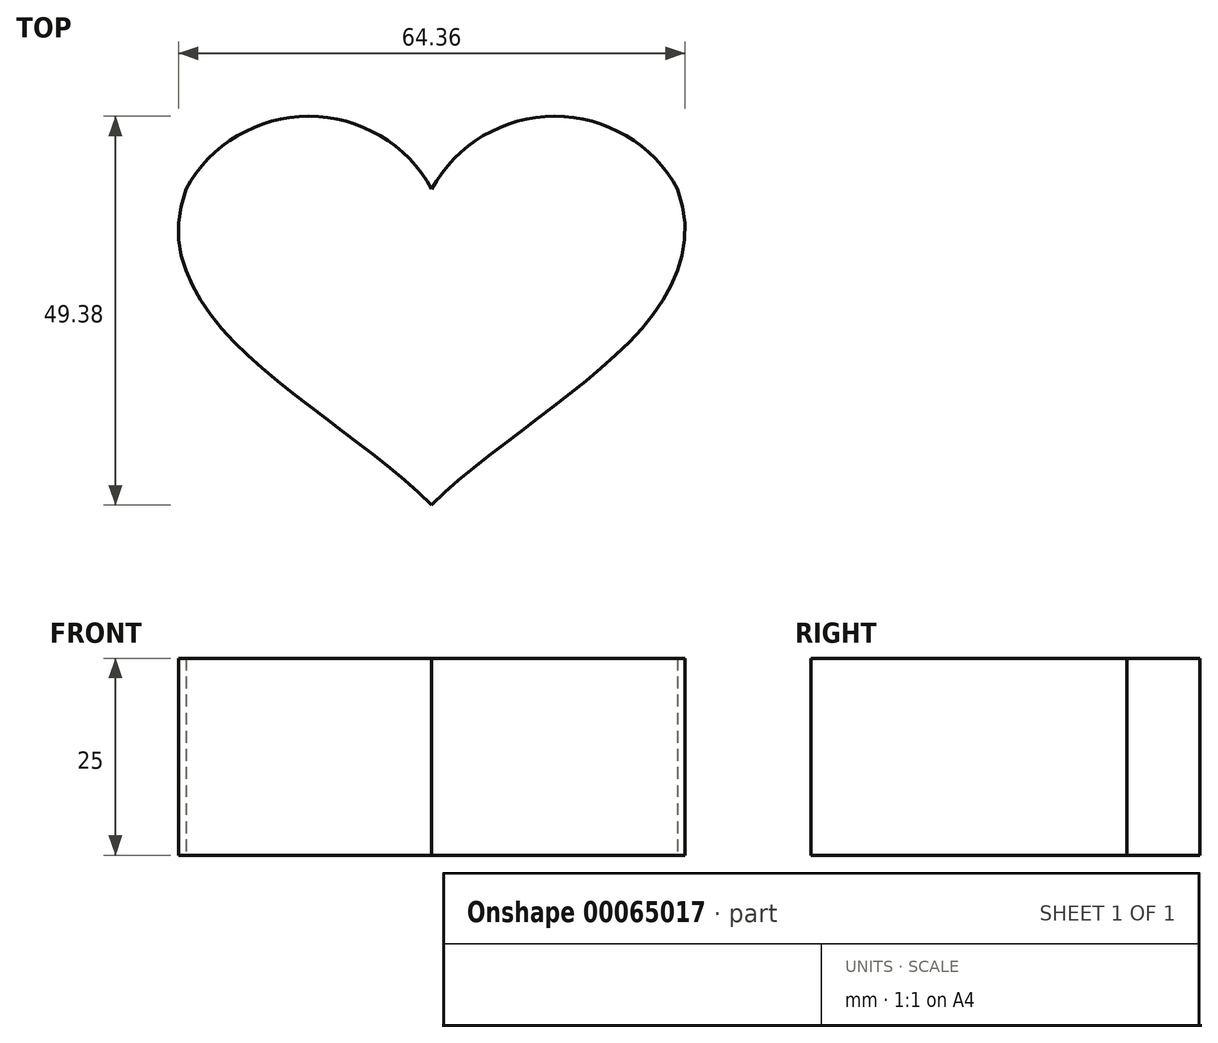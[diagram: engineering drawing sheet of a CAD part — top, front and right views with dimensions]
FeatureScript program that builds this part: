
annotation { "Feature Type Name" : "Feature", "Feature Type Description" : "" }
export const myFeature = defineFeature(function(context is Context, id is Id, definition is map)
    precondition{}
    {
        {
            var Q0;
            Q0=qCreatedBy(makeId("Top.planeOp"),FACE);
            var sketch = newSketch(context, id + "F0", { "sketchPlane" : qUnion([Q0])});
            skArc(sketch, "E0", {"start": v(0, 0) * mm, "mid": v(-15.62, 9.25) * mm, "end": v(-31.24, 0) * mm});
            skLineSegment(sketch, "E1", {"start": v(0, 0) * mm, "end": v(0, -40.13) * mm, "construction": true});
            skFitSpline(sketch, "E2", {"points": [v(-31.24, 0) * mm, v(0, -40.13) * mm], "startDerivative": vector(-18.35, -51.6) * mm, "endDerivative": vector(36.37, -36.7) * mm});
            skArc(sketch, "E3.MirrorCS", {"start": v(0, 0) * mm, "mid": v(15.62, 9.25) * mm, "end": v(31.24, 0) * mm});
            skFitSpline(sketch, "E4.MirrorCS", {"points": [v(31.24, 0) * mm, v(0, -40.13) * mm], "startDerivative": vector(18.35, -51.6) * mm, "endDerivative": vector(-36.37, -36.7) * mm});
            skSolve(sketch);
        }
        {
            var Q0;
            Q0 = qSketchRegion(id + "F0", true);
            extrude(context, id + "F1", {"entities" : qUnion([Q0]), "depth" : 25 * mm});
        }
    });
